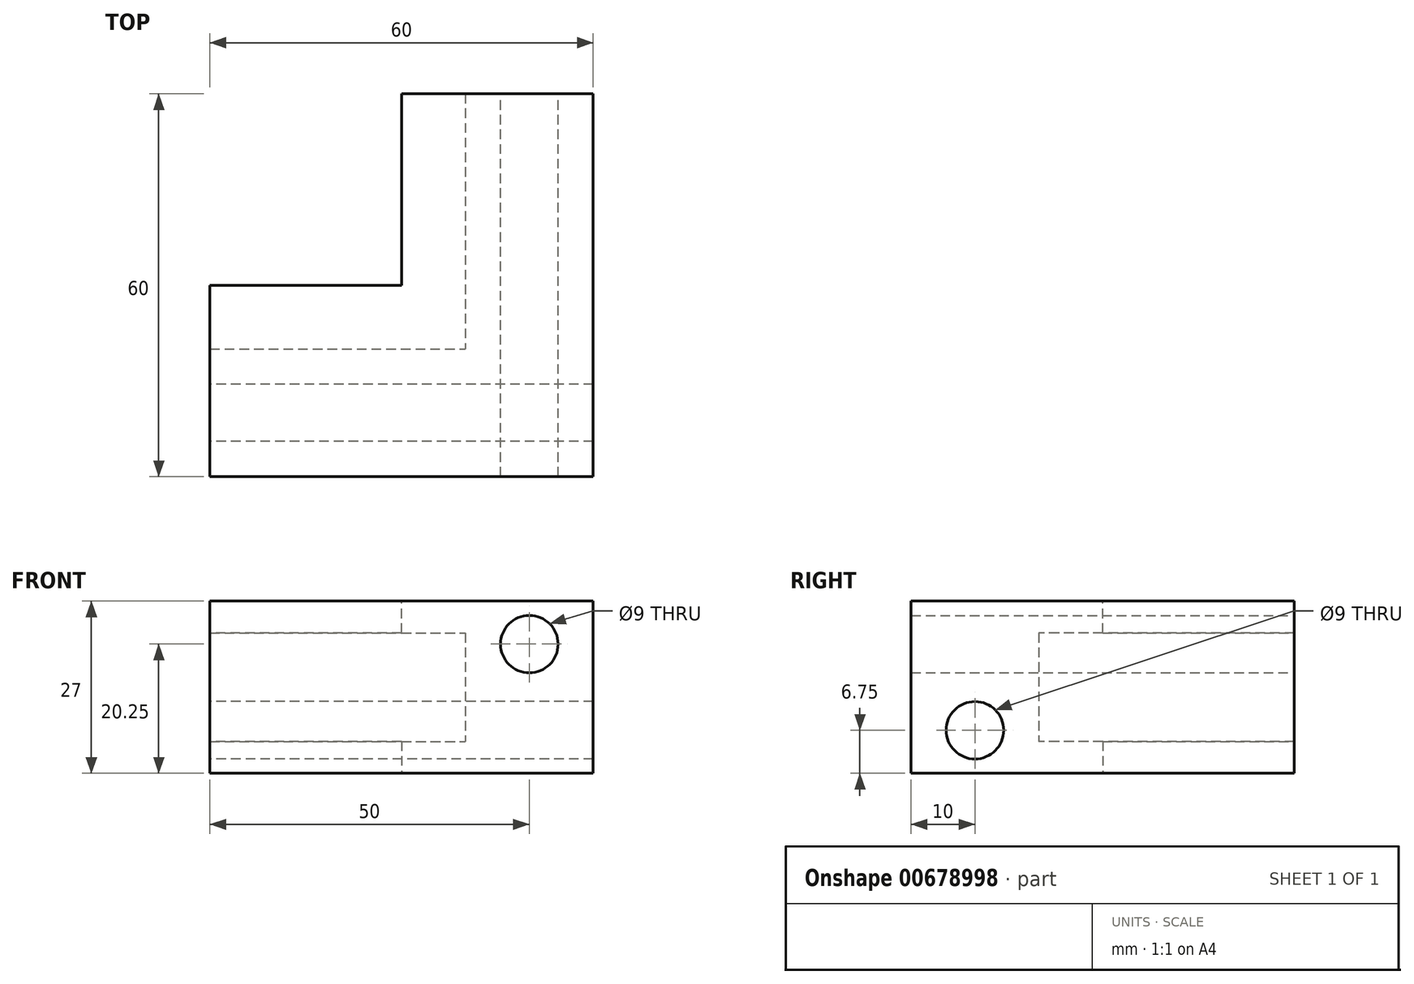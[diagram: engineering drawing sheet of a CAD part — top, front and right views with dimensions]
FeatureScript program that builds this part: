
annotation { "Feature Type Name" : "Feature", "Feature Type Description" : "" }
export const myFeature = defineFeature(function(context is Context, id is Id, definition is map)
    precondition{}
    {
        {
            var Q0;
            Q0=qCreatedBy(makeId("Top.planeOp"),FACE);
            var sketch = newSketch(context, id + "F0", { "sketchPlane" : qUnion([Q0])});
            skLineSegment(sketch, "E0.bottom", {"start": v(0, 0) * mm, "end": v(20, 0) * mm});
            skLineSegment(sketch, "E0.top", {"start": v(0, 30) * mm, "end": v(20, 30) * mm});
            skLineSegment(sketch, "E0.left", {"start": v(0, 0) * mm, "end": v(0, 30) * mm});
            skLineSegment(sketch, "E0.right", {"start": v(20, 0) * mm, "end": v(20, 30) * mm});
            skLineSegment(sketch, "E1.bottom", {"start": v(20, 0) * mm, "end": v(-30, 0) * mm});
            skLineSegment(sketch, "E1.top", {"start": v(20, -20) * mm, "end": v(-30, -20) * mm});
            skLineSegment(sketch, "E1.left", {"start": v(20, 0) * mm, "end": v(20, -20) * mm});
            skLineSegment(sketch, "E1.right", {"start": v(-30, 0) * mm, "end": v(-30, -20) * mm});
            skLineSegment(sketch, "E2", {"start": v(-30, -10) * mm, "end": v(10, -10) * mm});
            skLineSegment(sketch, "E3", {"start": v(10, 30) * mm, "end": v(10, -10) * mm});
            skLineSegment(sketch, "E4", {"start": v(-5, -20) * mm, "end": v(-5, -10) * mm});
            skSolve(sketch);
        }
        {
            var Q0;
            {var subQ1=sQuery(id+"F0.wireOp",EDGE,"E1.top");Q0=makeQuery(id+"F0.imprint","IMPRINT",FACE,{"disambiguationData":[TD([[makeQuery(id+"F0.imprint","IMPRINT",EDGE,{"derivedFrom":subQ1}),-1.0]])]});}
            var Q1;
            {var subQ0=sQuery(id+"F0.wireOp",EDGE,"E0.right");Q1=makeQuery(id+"F0.imprint","IMPRINT",FACE,{"disambiguationData":[TD([[makeQuery(id+"F0.imprint","IMPRINT",EDGE,{"derivedFrom":subQ0}),1.0]])]});}
            var Q2;
            {var subQ4=sQuery(id+"F0.wireOp",EDGE,"E1.left");Q2=makeQuery(id+"F0.imprint","IMPRINT",FACE,{"disambiguationData":[TD([[makeQuery(id+"F0.imprint","IMPRINT",EDGE,{"derivedFrom":subQ4}),-1.0]])]});}
            extrude(context, id + "F1", {"entities" : qUnion([Q0, Q1, Q2]), "depth" : 27 * mm, "offsetDistance" : 25 * mm});
        }
        {
            var Q0;
            Q0=makeQuery(id+"F1.opExtrude","SWEPT_FACE",FACE,{"disambiguationData":[OSD([sQuery(id+"F0.wireOp",EDGE,"E3")])]});
            var sketch = newSketch(context, id + "F2", { "sketchPlane" : qUnion([Q0])});
            skLineSegment(sketch, "E5", {"start": v(-30, 13.5) * mm, "end": v(10, 13.5) * mm});
            skSolve(sketch);
        }
        {
            var Q0;
            {var subQ0=sQuery(id+"F0.wireOp",EDGE,"E0.left");Q0=makeQuery(id+"F0.imprint","IMPRINT",FACE,{"disambiguationData":[TD([[makeQuery(id+"F0.imprint","IMPRINT",EDGE,{"derivedFrom":subQ0}),-1.0]])]});}
            var Q1;
            {var subQ3=sQuery(id+"F0.wireOp",EDGE,"E2");Q1=makeQuery(id+"F0.imprint","IMPRINT",FACE,{"disambiguationData":[TD([[makeQuery(id+"F0.imprint","IMPRINT",EDGE,{"derivedFrom":subQ3}),1.0]])]});}
            extrude(context, id + "F3", {"entities" : qUnion([Q0, Q1]), "operationType" : NewBodyOperationType.ADD, "depth" : 5 * mm, "offsetDistance" : 25 * mm});
        }
        {
            var Q0;
            Q0=sQuery(id+"F2.wireOp",EDGE,"E5");
            cPlane(context, id + "F4", {"entities" : qUnion([Q0]), "cplaneType" : CPlaneType.LINE_ANGLE, "offset" : 25 * mm, "angle" : 0 * degree, "width" : 150 * mm, "height" : 150 * mm});
        }
        {
            var Q0;
            Q0=makeQuery(id+"F1.opExtrude","CAP_FACE",FACE,{"disambiguationData":[OSD([sQuery(id+"F0.wireOp",EDGE,"E0.top"),sQuery(id+"F0.wireOp",EDGE,"E0.right"),sQuery(id+"F0.wireOp",EDGE,"E1.top"),sQuery(id+"F0.wireOp",EDGE,"E1.left"),sQuery(id+"F0.wireOp",EDGE,"E1.right"),sQuery(id+"F0.wireOp",EDGE,"E2"),sQuery(id+"F0.wireOp",EDGE,"E3")])],"isStart":false});
            var Q1;
            Q1=qCreatedBy(id+"F4.planeOp",FACE);
            extrude(context, id + "F5", {"entities" : qUnion([Q0]), "operationType" : NewBodyOperationType.REMOVE, "endBound" : BoundingType.UP_TO_SURFACE, "oppositeDirection" : true, "depth" : 25 * mm, "endBoundEntityFace" : qUnion([Q1]), "offsetDistance" : 25 * mm});
        }
        {
            var Q0;
            Q0=makeQuery(id+"F1.opExtrude","SWEPT_BODY",BODY,{"disambiguationData":[OSD([sQuery(id+"F0.wireOp",EDGE,"E0.top"),sQuery(id+"F0.wireOp",EDGE,"E0.right"),sQuery(id+"F0.wireOp",EDGE,"E1.top"),sQuery(id+"F0.wireOp",EDGE,"E1.left"),sQuery(id+"F0.wireOp",EDGE,"E1.right"),sQuery(id+"F0.wireOp",EDGE,"E2"),sQuery(id+"F0.wireOp",EDGE,"E3")])]});
            var Q1;
            Q1=qCreatedBy(id+"F4.planeOp",FACE);
            mirror(context, id + "F6", {"operationType" : NewBodyOperationType.ADD, "entities" : qUnion([Q0]), "mirrorPlane" : qUnion([Q1])});
        }
        {
            var Q0;
            {var subQ0=makeQuery(id+"F1.opExtrude","SWEPT_FACE",FACE,{"disambiguationData":[OSD([sQuery(id+"F0.wireOp",EDGE,"E1.top")])]});Q0=makeQuery(id+"F6.boolean.opBoolean","MERGE",FACE,{"derivedFrom":[subQ0,makeQuery(id+"F6.opPattern","COPY",FACE,{"derivedFrom":subQ0,"instanceName":"1"})]});}
            extrude(context, id + "F7", {"entities" : qUnion([Q0]), "operationType" : NewBodyOperationType.ADD, "depth" : 10 * mm, "offsetDistance" : 25 * mm});
        }
        {
            var Q0;
            {var subQ0=sQuery(id+"F0.wireOp",EDGE,"E1.left");var subQ1=makeQuery(id+"F1.opExtrude","SWEPT_FACE",FACE,{"disambiguationData":[OSD([sQuery(id+"F0.wireOp",EDGE,"E0.right"),subQ0])]});Q0=makeQuery(id+"F7.boolean.opBoolean","MERGE",FACE,{"derivedFrom":[makeQuery(id+"F6.boolean.opBoolean","MERGE",FACE,{"derivedFrom":[subQ1,makeQuery(id+"F6.opPattern","COPY",FACE,{"derivedFrom":subQ1,"instanceName":"1"})]}),makeQuery(id+"F7.opExtrude","SWEPT_FACE",FACE,{"disambiguationData":[OSD([sQuery(id+"F0.wireOp",EDGE,"E1.top"),subQ0])]})]});}
            extrude(context, id + "F8", {"entities" : qUnion([Q0]), "operationType" : NewBodyOperationType.ADD, "depth" : 10 * mm, "offsetDistance" : 25 * mm});
        }
        {
            var Q0;
            {var subQ0=sQuery(id+"F0.wireOp",EDGE,"E0.top");var subQ1=makeQuery(id+"F3.boolean.opBoolean","MERGE",FACE,{"derivedFrom":[makeQuery(id+"F1.opExtrude","SWEPT_FACE",FACE,{"disambiguationData":[OSD([subQ0])]}),makeQuery(id+"F3.opExtrude","SWEPT_FACE",FACE,{"disambiguationData":[OSD([subQ0])]})]});Q0=makeQuery(id+"F8.boolean.opBoolean","MERGE",FACE,{"derivedFrom":[makeQuery(id+"F6.boolean.opBoolean","MERGE",FACE,{"derivedFrom":[subQ1,makeQuery(id+"F6.opPattern","COPY",FACE,{"derivedFrom":subQ1,"instanceName":"1"})]}),makeQuery(id+"F8.opExtrude","SWEPT_FACE",FACE,{"disambiguationData":[OSD([subQ0,sQuery(id+"F0.wireOp",EDGE,"E0.right")])]})]});}
            var sketch = newSketch(context, id + "F9", { "sketchPlane" : qUnion([Q0])});
            skLineSegment(sketch, "E6", {"start": v(-10, 27) * mm, "end": v(-10, 0) * mm});
            skCircle(sketch, "E7", {"center": v(-20, 20.25) * mm, "radius": 4.5 * mm});
            skSolve(sketch);
        }
        {
            var Q0;
            Q0=makeQuery(id+"F9.imprint","IMPRINT",FACE,{"disambiguationData":[TD([[makeQuery(id+"F9.imprint","IMPRINT",EDGE,{"derivedFrom":sQuery(id+"F9.wireOp",EDGE,"E7")}),1.0]])]});
            extrude(context, id + "F10", {"entities" : qUnion([Q0]), "operationType" : NewBodyOperationType.REMOVE, "endBound" : BoundingType.UP_TO_NEXT, "oppositeDirection" : true, "depth" : 25 * mm, "offsetDistance" : 25 * mm});
        }
        {
            var Q0;
            {var subQ0=sQuery(id+"F0.wireOp",EDGE,"E1.right");var subQ1=makeQuery(id+"F3.boolean.opBoolean","MERGE",FACE,{"derivedFrom":[makeQuery(id+"F1.opExtrude","SWEPT_FACE",FACE,{"disambiguationData":[OSD([subQ0])]}),makeQuery(id+"F3.opExtrude","SWEPT_FACE",FACE,{"disambiguationData":[OSD([subQ0])]})]});Q0=makeQuery(id+"F7.boolean.opBoolean","MERGE",FACE,{"derivedFrom":[makeQuery(id+"F6.boolean.opBoolean","MERGE",FACE,{"derivedFrom":[subQ1,makeQuery(id+"F6.opPattern","COPY",FACE,{"derivedFrom":subQ1,"instanceName":"1"})]}),makeQuery(id+"F7.opExtrude","SWEPT_FACE",FACE,{"disambiguationData":[OSD([sQuery(id+"F0.wireOp",EDGE,"E1.top"),subQ0])]})]});}
            var sketch = newSketch(context, id + "F11", { "sketchPlane" : qUnion([Q0])});
            skLineSegment(sketch, "E8", {"start": v(30, 13.5) * mm, "end": v(10, 13.5) * mm});
            skLineSegment(sketch, "E9", {"start": v(20, 13.5) * mm, "end": v(20, 0) * mm});
            skCircle(sketch, "E10", {"center": v(20, 6.75) * mm, "radius": 4.5 * mm});
            skSolve(sketch);
        }
        {
            var Q0;
            {var subQ0=sQuery(id+"F11.wireOp",EDGE,"E10");var subQ1=sQuery(id+"F11.wireOp",EDGE,"E9");var subQ2=makeQuery(id+"F11.imprint","INTERSECT",VERTEX,{"disambiguationData":[OD(0.0)],"derivedFrom":[subQ1,subQ0]});Q0=makeQuery(id+"F11.imprint","IMPRINT",FACE,{"disambiguationData":[TD([[makeQuery(id+"F11.imprint","IMPRINT",EDGE,{"disambiguationData":[TD([[subQ2,-1.0]])],"derivedFrom":subQ1}),1.0]])]});}
            var Q1;
            {var subQ0=sQuery(id+"F11.wireOp",EDGE,"E10");var subQ1=sQuery(id+"F11.wireOp",EDGE,"E9");var subQ2=makeQuery(id+"F11.imprint","INTERSECT",VERTEX,{"disambiguationData":[OD(0.0)],"derivedFrom":[subQ1,subQ0]});Q1=makeQuery(id+"F11.imprint","IMPRINT",FACE,{"disambiguationData":[TD([[makeQuery(id+"F11.imprint","IMPRINT",EDGE,{"disambiguationData":[TD([[subQ2,-1.0]])],"derivedFrom":subQ1}),-1.0]])]});}
            extrude(context, id + "F12", {"entities" : qUnion([Q0, Q1]), "operationType" : NewBodyOperationType.REMOVE, "endBound" : BoundingType.THROUGH_ALL, "oppositeDirection" : true, "depth" : 25 * mm, "offsetDistance" : 25 * mm});
        }
    });
